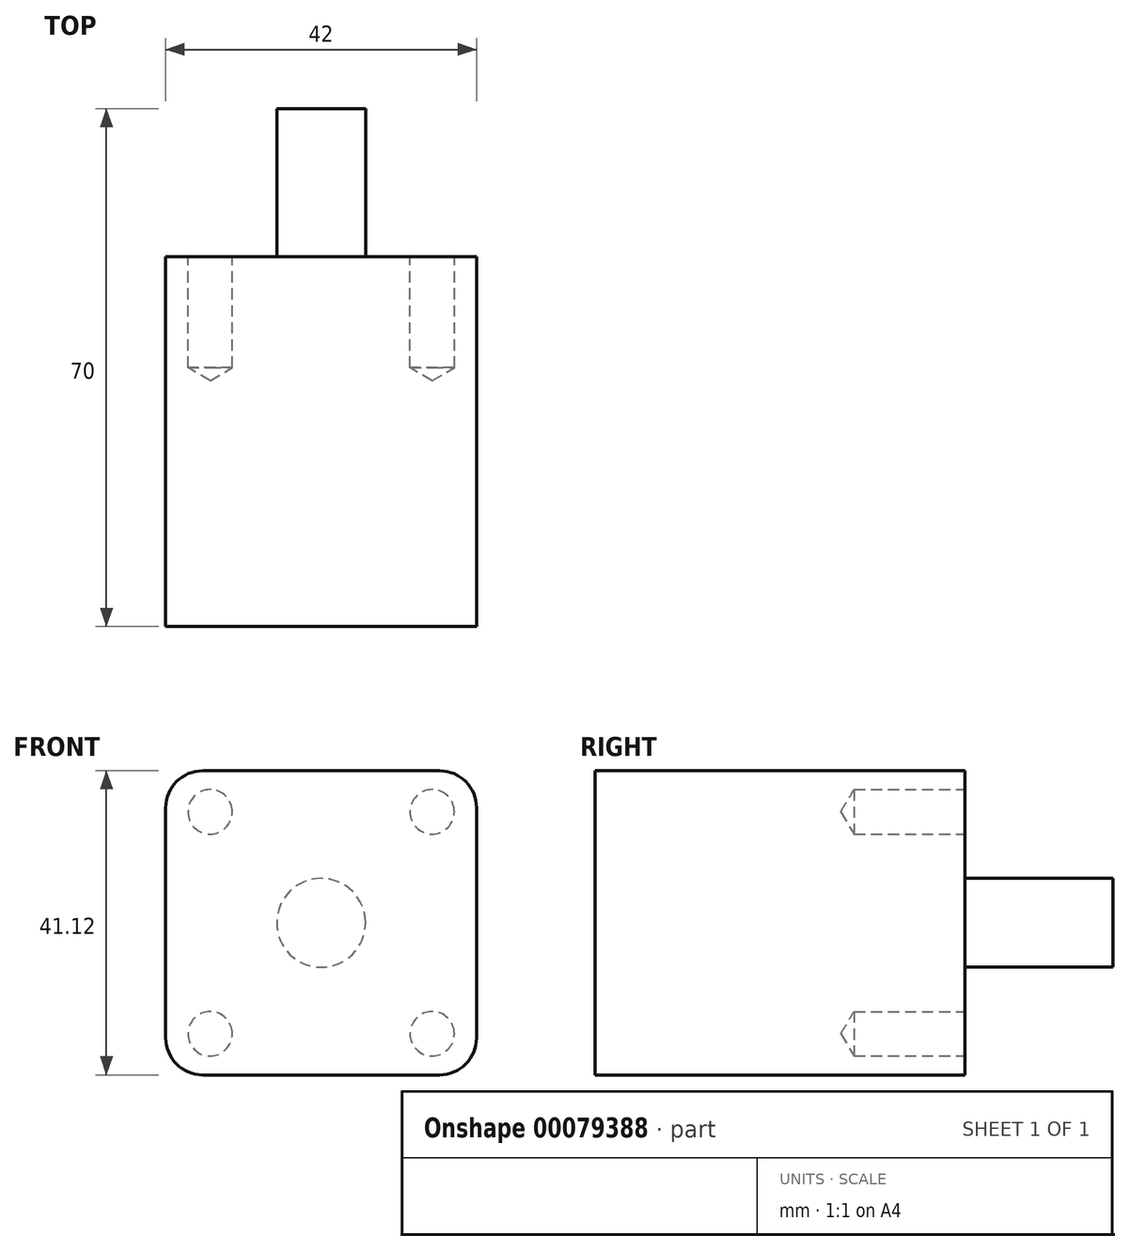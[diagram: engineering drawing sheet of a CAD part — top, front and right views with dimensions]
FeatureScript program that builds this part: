
annotation { "Feature Type Name" : "Feature", "Feature Type Description" : "" }
export const myFeature = defineFeature(function(context is Context, id is Id, definition is map)
    precondition{}
    {
        {
            var Q0;
            Q0=qCreatedBy(makeId("Front.planeOp"),FACE);
            var sketch = newSketch(context, id + "F0", { "sketchPlane" : qUnion([Q0])});
            skLineSegment(sketch, "E0.bottom", {"start": v(21, 20.56) * mm, "end": v(-21, 20.56) * mm});
            skLineSegment(sketch, "E0.top", {"start": v(21, -20.56) * mm, "end": v(-21, -20.56) * mm});
            skLineSegment(sketch, "E0.left", {"start": v(21, 20.56) * mm, "end": v(21, -20.56) * mm});
            skLineSegment(sketch, "E0.right", {"start": v(-21, 20.56) * mm, "end": v(-21, -20.56) * mm});
            skPoint(sketch, "E0.middle", {"position": v(0, 0) * mm});
            skCircle(sketch, "E1", {"center": v(0, 0) * mm, "radius": 6 * mm});
            skCircle(sketch, "E2", {"center": v(-15, 15) * mm, "radius": 3 * mm});
            skCircle(sketch, "E3", {"center": v(15, 15) * mm, "radius": 3 * mm});
            skCircle(sketch, "E4", {"center": v(-15, -15) * mm, "radius": 3 * mm});
            skCircle(sketch, "E5", {"center": v(15, -15) * mm, "radius": 3 * mm});
            skSolve(sketch);
        }
        {
            var Q0;
            Q0=makeQuery(id+"F0.imprint","IMPRINT",FACE,{"disambiguationData":[TD([[makeQuery(id+"F0.imprint","IMPRINT",EDGE,{"derivedFrom":sQuery(id+"F0.wireOp",EDGE,"E0.bottom")}),1.0]])]});
            var Q1;
            Q1=makeQuery(id+"F0.imprint","IMPRINT",FACE,{"disambiguationData":[TD([[makeQuery(id+"F0.imprint","IMPRINT",EDGE,{"derivedFrom":sQuery(id+"F0.wireOp",EDGE,"E5")}),1.0]])]});
            var Q2;
            Q2=makeQuery(id+"F0.imprint","IMPRINT",FACE,{"disambiguationData":[TD([[makeQuery(id+"F0.imprint","IMPRINT",EDGE,{"derivedFrom":sQuery(id+"F0.wireOp",EDGE,"E1")}),1.0]])]});
            var Q3;
            Q3=makeQuery(id+"F0.imprint","IMPRINT",FACE,{"disambiguationData":[TD([[makeQuery(id+"F0.imprint","IMPRINT",EDGE,{"derivedFrom":sQuery(id+"F0.wireOp",EDGE,"E3")}),1.0]])]});
            var Q4;
            Q4=makeQuery(id+"F0.imprint","IMPRINT",FACE,{"disambiguationData":[TD([[makeQuery(id+"F0.imprint","IMPRINT",EDGE,{"derivedFrom":sQuery(id+"F0.wireOp",EDGE,"E2")}),1.0]])]});
            var Q5;
            Q5=makeQuery(id+"F0.imprint","IMPRINT",FACE,{"disambiguationData":[TD([[makeQuery(id+"F0.imprint","IMPRINT",EDGE,{"derivedFrom":sQuery(id+"F0.wireOp",EDGE,"E4")}),1.0]])]});
            extrude(context, id + "F1", {"entities" : qUnion([Q0, Q1, Q2, Q3, Q4, Q5]), "depth" : 50 * mm});
        }
        {
            var Q0;
            Q0=makeQuery(id+"F0.imprint","IMPRINT",FACE,{"disambiguationData":[TD([[makeQuery(id+"F0.imprint","IMPRINT",EDGE,{"derivedFrom":sQuery(id+"F0.wireOp",EDGE,"E1")}),1.0]])]});
            extrude(context, id + "F2", {"entities" : qUnion([Q0]), "oppositeDirection" : true, "depth" : 20 * mm});
        }
        {
            var Q0;
            Q0=sQuery(id+"F0.wireOp",VERTEX,"E5.center");
            var Q1;
            Q1=sQuery(id+"F0.wireOp",VERTEX,"E3.center");
            var Q2;
            Q2=sQuery(id+"F0.wireOp",VERTEX,"E2.center");
            var Q3;
            Q3=sQuery(id+"F0.wireOp",VERTEX,"E4.center");
            var Q4;
            Q4=makeQuery(id+"F1.opExtrude","SWEPT_BODY",BODY,{"disambiguationData":[OSD([sQuery(id+"F0.wireOp",EDGE,"E0.bottom"),sQuery(id+"F0.wireOp",EDGE,"E0.top"),sQuery(id+"F0.wireOp",EDGE,"E0.left"),sQuery(id+"F0.wireOp",EDGE,"E0.right")])]});
            hole(context, id + "F3", {"style" : HoleStyle.SIMPLE, "endStyle" : HoleEndStyle.BLIND, "oppositeDirection" : true, "holeDiameter" : 6 * mm, "holeDepth" : 15 * mm, "locations" : qUnion([Q0, Q1, Q2, Q3]), "scope" : qUnion([Q4])});
        }
        {
            var Q0;
            Q0=makeQuery(id+"F1.opExtrude","SWEPT_EDGE",EDGE,{"disambiguationData":[OSD([sQuery(id+"F0.wireOp",EDGE,"E0.top"),sQuery(id+"F0.wireOp",EDGE,"E0.left")])]});
            var Q1;
            Q1=makeQuery(id+"F1.opExtrude","SWEPT_EDGE",EDGE,{"disambiguationData":[OSD([sQuery(id+"F0.wireOp",EDGE,"E0.bottom"),sQuery(id+"F0.wireOp",EDGE,"E0.left")])]});
            var Q2;
            Q2=makeQuery(id+"F1.opExtrude","SWEPT_EDGE",EDGE,{"disambiguationData":[OSD([sQuery(id+"F0.wireOp",EDGE,"E0.top"),sQuery(id+"F0.wireOp",EDGE,"E0.right")])]});
            var Q3;
            Q3=makeQuery(id+"F1.opExtrude","SWEPT_EDGE",EDGE,{"disambiguationData":[OSD([sQuery(id+"F0.wireOp",EDGE,"E0.bottom"),sQuery(id+"F0.wireOp",EDGE,"E0.right")])]});
            fillet(context, id + "F4", {"entities" : qUnion([Q0, Q1, Q2, Q3]), "radius" : 5 * mm, "tangentPropagation" : true, "allowEdgeOverflow" : false});
        }
    });
